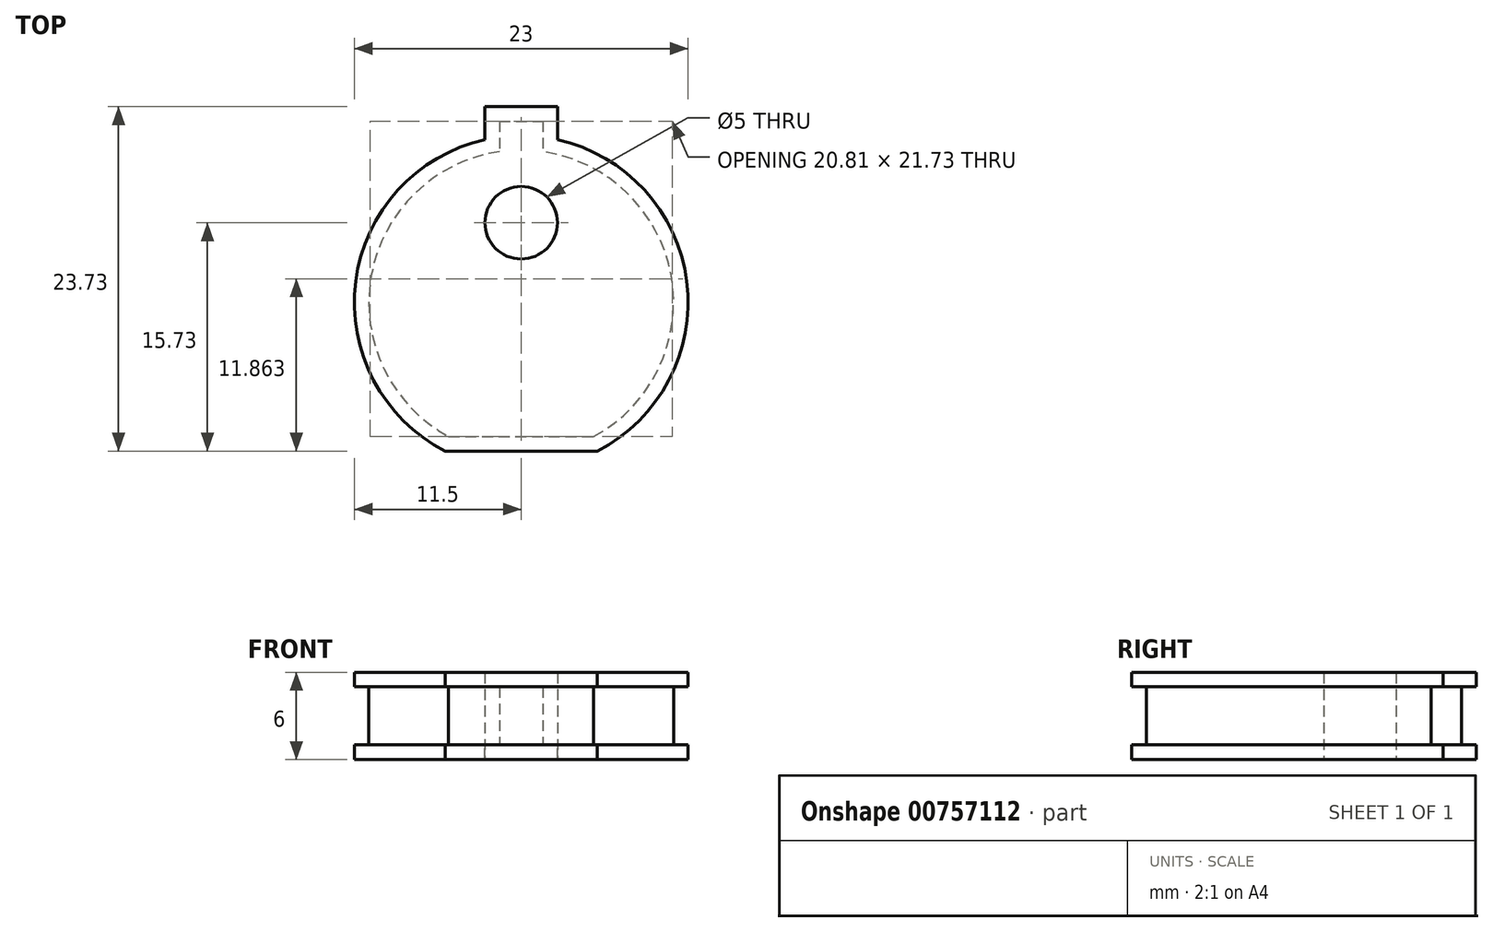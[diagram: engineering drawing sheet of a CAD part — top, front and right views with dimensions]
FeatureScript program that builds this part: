
annotation { "Feature Type Name" : "Feature", "Feature Type Description" : "" }
export const myFeature = defineFeature(function(context is Context, id is Id, definition is map)
    precondition{}
    {
        {
            var Q0;
            Q0=qCreatedBy(makeId("Top.planeOp"),FACE);
            var sketch = newSketch(context, id + "F0", { "sketchPlane" : qUnion([Q0])});
            skArc(sketch, "E0", {"start": v(5, -9.23) * mm, "mid": v(0, 10.5) * mm, "end": v(-5, -9.23) * mm});
            skCircle(sketch, "E1", {"center": v(0, 5.5) * mm, "radius": 2.5 * mm});
            skLineSegment(sketch, "E2", {"start": v(-5, -9.23) * mm, "end": v(5, -9.23) * mm});
            skCircle(sketch, "E3", {"center": v(0, 0) * mm, "radius": 12.5 * mm, "construction": true});
            skLineSegment(sketch, "E4", {"start": v(-1.5, 12.5) * mm, "end": v(1.5, 12.5) * mm});
            skLineSegment(sketch, "E5", {"start": v(0, 5.5) * mm, "end": v(0, 12.5) * mm, "construction": true});
            skLineSegment(sketch, "E6", {"start": v(1.5, 12.5) * mm, "end": v(1.5, 7.5) * mm});
            skLineSegment(sketch, "E7", {"start": v(-1.5, 12.5) * mm, "end": v(-1.5, 7.5) * mm});
            skSolve(sketch);
        }
        {
            var Q0;
            Q0 = qSketchRegion(id + "F0", true);
            extrude(context, id + "F1", {"entities" : qUnion([Q0]), "depth" : 4 * mm, "offsetDistance" : 25 * mm});
        }
        {
            var Q0;
            Q0=makeQuery(id+"F1.opExtrude","CAP_FACE",FACE,{"disambiguationData":[OSD([sQuery(id+"F0.wireOp",EDGE,"E0"),sQuery(id+"F0.wireOp",EDGE,"E1"),sQuery(id+"F0.wireOp",EDGE,"E2"),sQuery(id+"F0.wireOp",EDGE,"E4"),sQuery(id+"F0.wireOp",EDGE,"E6"),sQuery(id+"F0.wireOp",EDGE,"E7")])],"isStart":false});
            var sketch = newSketch(context, id + "F2", { "sketchPlane" : qUnion([Q0])});
            skLineSegment(sketch, "E8.0", {"start": v(-2.5, 13.5) * mm, "end": v(-2.5, 11.22) * mm});
            skLineSegment(sketch, "E8.1", {"start": v(-5.25, -10.23) * mm, "end": v(5.25, -10.23) * mm});
            skArc(sketch, "E8.2", {"start": v(5.25, -10.23) * mm, "mid": v(11.4, 1.46) * mm, "end": v(2.5, 11.22) * mm});
            skArc(sketch, "E8.3", {"start": v(-2.5, 11.22) * mm, "mid": v(-11.4, 1.46) * mm, "end": v(-5.25, -10.23) * mm});
            skLineSegment(sketch, "E8.4", {"start": v(2.5, 13.5) * mm, "end": v(2.5, 11.22) * mm});
            skLineSegment(sketch, "E8.5", {"start": v(-2.5, 13.5) * mm, "end": v(2.5, 13.5) * mm});
            skSolve(sketch);
        }
        {
            var Q0;
            Q0=makeQuery(id+"F1.opExtrude","CAP_FACE",FACE,{"disambiguationData":[OSD([sQuery(id+"F0.wireOp",EDGE,"E0"),sQuery(id+"F0.wireOp",EDGE,"E1"),sQuery(id+"F0.wireOp",EDGE,"E2"),sQuery(id+"F0.wireOp",EDGE,"E4"),sQuery(id+"F0.wireOp",EDGE,"E6"),sQuery(id+"F0.wireOp",EDGE,"E7")])],"isStart":true});
            var sketch = newSketch(context, id + "F3", { "sketchPlane" : qUnion([Q0])});
            skLineSegment(sketch, "E9.0", {"start": v(-5.25, 10.23) * mm, "end": v(5.25, 10.23) * mm});
            skLineSegment(sketch, "E9.1", {"start": v(2.5, -13.5) * mm, "end": v(2.5, -11.22) * mm});
            skLineSegment(sketch, "E9.2", {"start": v(-2.5, -13.5) * mm, "end": v(2.5, -13.5) * mm});
            skArc(sketch, "E9.3", {"start": v(5.25, 10.23) * mm, "mid": v(11.4, -1.46) * mm, "end": v(2.5, -11.22) * mm});
            skLineSegment(sketch, "E9.4", {"start": v(-2.5, -13.5) * mm, "end": v(-2.5, -11.22) * mm});
            skArc(sketch, "E9.5", {"start": v(-2.5, -11.22) * mm, "mid": v(-11.4, -1.46) * mm, "end": v(-5.25, 10.23) * mm});
            skSolve(sketch);
        }
        {
            var Q0;
            Q0 = qSketchRegion(id + "F2", true);
            extrude(context, id + "F4", {"entities" : qUnion([Q0]), "operationType" : NewBodyOperationType.ADD, "depth" : 1 * mm, "offsetDistance" : 25 * mm});
        }
        {
            var Q0;
            Q0 = qSketchRegion(id + "F3", true);
            extrude(context, id + "F5", {"entities" : qUnion([Q0]), "operationType" : NewBodyOperationType.ADD, "depth" : 1 * mm, "offsetDistance" : 25 * mm});
        }
        {
            var Q0;
            Q0=qCreatedBy(makeId("Top.planeOp"),FACE);
            var sketch = newSketch(context, id + "F6", { "sketchPlane" : qUnion([Q0])});
            skCircle(sketch, "E10", {"center": v(0, 5.5) * mm, "radius": 2.5 * mm});
            skSolve(sketch);
        }
        {
            var Q0;
            Q0 = qSketchRegion(id + "F6", true);
            extrude(context, id + "F7", {"entities" : qUnion([Q0]), "operationType" : NewBodyOperationType.REMOVE, "endBound" : BoundingType.THROUGH_ALL, "oppositeDirection" : true, "depth" : 25 * mm, "offsetDistance" : 25 * mm, "hasSecondDirection" : true, "secondDirectionBound" : SecondDirectionBoundingType.THROUGH_ALL, "secondDirectionOppositeDirection" : false, "secondDirectionDepth" : 25 * mm});
        }
    });
